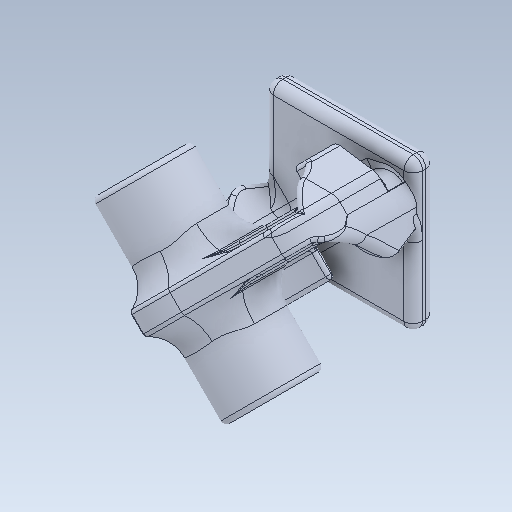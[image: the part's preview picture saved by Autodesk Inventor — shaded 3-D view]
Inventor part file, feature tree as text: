
AUTODESK INVENTOR PART (.ipt)
format: ipt  version: 2020 (Build 240168000, 168)  size: 1,209,856 bytes
history: native  units: in
note: dims shown in document units (in); Inventor stores cm internally (conversion verified against a paired STEP export)
features: fillet x1
ambient origin geometry x8: Origin, YZ Plane, XZ Plane, XY Plane, X Axis, Y Axis, Z Axis, Center Point
bodies: Solid1 (feature_tree)
feature tree (1):
  fillet  "Fillet119"  [1 undecoded]
note: 1 required parameter value undecoded (feature->parameter linkage not recoverable at this tier; creation-order binding heuristic only, values carry confidence <= 0.55)
